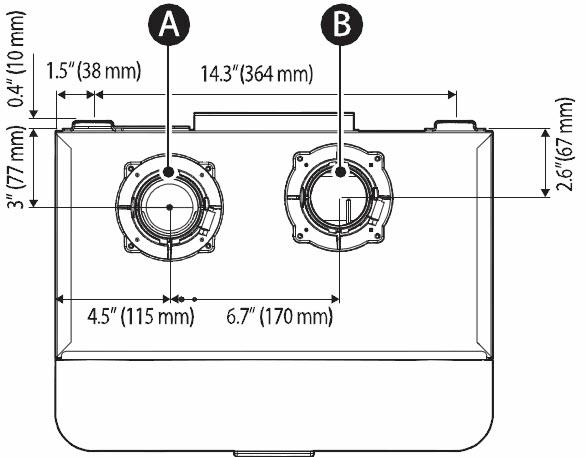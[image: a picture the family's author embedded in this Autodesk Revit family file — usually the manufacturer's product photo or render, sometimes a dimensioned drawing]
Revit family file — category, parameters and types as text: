
# Revit family: Water_Heater-Racks-Navien-NPE-4_Unit_Front-Wall-02
name_source: partatom
category: Mechanical Equipment
revit_build: Autodesk Revit 2016 (Build: 20150220_1215(x64)
units: mm (PartAtom-declared; Revit-internal decimal feet)

## family parameters
Cut with Voids When Loaded = No
Host = Face
OmniClass Number = 23.65.35.11
OmniClass Title = Supply Water Heaters
Part Type = Normal
Room Calculation Point = No
Round Connector Dimension = Use Diameter
Shared = No

## types (4) — shared parameters
2" Exhaust/Intake = Yes
3" Exhaust/Intake = No
Apparent Load = 0 VA
Assembly Code = D3010500
Certifications = Energy Star | AHRI | CSA | CSA | NFS
Cold Water Inlet = 1"
Configuration = NPE_F4_4F
Default Elevation = 48 "
Depth = 23.8 "
Description = 4 Unit Front
Exhaust = 2"
Finish = Metal - Navien - White
Flow Rate = 1 GPM
Flow Rate Note = 35°F (19°C) temp rise: 11.2 GPM (42 L/m) | 45°F (25°C) temp rise: 8.7 GPM (33 L/m) | 67°F (36°C) temp rise: NPE-240A: 5.6 GPM(21 L/m), NPE-240S: 5.7 GPM(22 L/m)
Frequency = 60 Hz
Gas Inlet = 1"
Heating Capacity = 120000.0 Btu/h
Heating Capacity Note = 19,900–199,900 (BTU/H)
Height = 65.5 "
Hot Water Outlet = 1"
Ignition = Electronic ignition
Installation Type = Indoor
Intake = 2"
Keynote = 22 33 00.A1
Manifold(s) = (1) 30019043A
Manufacturer = Navien, Inc.
Manufacturer Fax Number = (949) 420-0430
Natural Gas Manifold Pressure = -0.05" WC to -0.58" WC
Natural Gas Supply Pressure = 3.5"–10.5" WC
Number of Poles = 1
Phase = 1
Power Factor = 1
Product Documentation Link = https://www.navieninc.com
Product Name = NPE Series Tankless Water Heaters w/ Racks
Product Page URL = https://www.navieninc.com
Propane Gas Manifold Pressure = -0.10" WC to -0.78" WC
Propane Gas Supply Pressure = 8"–13" WC
Required Cascade Operation Accessory = (4) 30014367A (Common Vent Damper & Cascade Communication Cable) or (3) GXXX000546 (Individual Vent Cascade Communication Cable)
Type Comments = For Wall Mount RL Manifold systems- Exclude Base & Add-on Racks
URL = https://www.navieninc.com
Venting = Exhaust: 2" PVC, CPVC, PP, SS / 2" special gas vent type BH (Class II, A/B/C) | Intake: 2" PVC, CPVC, PP, SS / 2" special gas vent type BH (Class II, A/B/C) | Vent clearances: 0" to combustibles
Venting Type = Forced draft direct vent
Version = 2016 - v1.0.a
Voltage = 120 V
Water Pressure = 15–150 PSI
Wi-Fi Ready = NaviLink Wi-Fi Control: PBCM-AS-001
Width = 82.3 "

## per-type parameters (varying)
| type | Constraints | Model | Natural Gas | Propane Gas | Recirculation Inlet | Recirculation Inlet Visibility | Tankless Water Heaters | Weight |
| Natural Gas - Recirculating System - NPE-240A(Advanced)-NG | 6 | (4) NPE-240A-NG | Yes | No | 0" | Yes | (4) NPE-240A-NG | 82.00 lbf |
| Natural Gas - NPE-240S(Standard)-NG | 7 | (4) NPE-240S-NG | Yes | No | 1" | No | (4) NPE-240S-NG | 75.00 lbf |
| Propane Gas - Recirculating System - NPE-240A(Advanced)-LPG | 6 | (4) NPE-240A-LPG | No | Yes | 0" | Yes | (4) NPE-240A-LPG | 82.00 lbf |
| Propane Gas - NPE-240S(Standard)-LPG | 7 | (4) NPE-240S-LPG | No | Yes | 1" | No | (4) NPE-240S-LPG | 75.00 lbf |

## geometry (parser evidence)
native form markers: Sweep x10
no freeform markers — native parametric forms only
